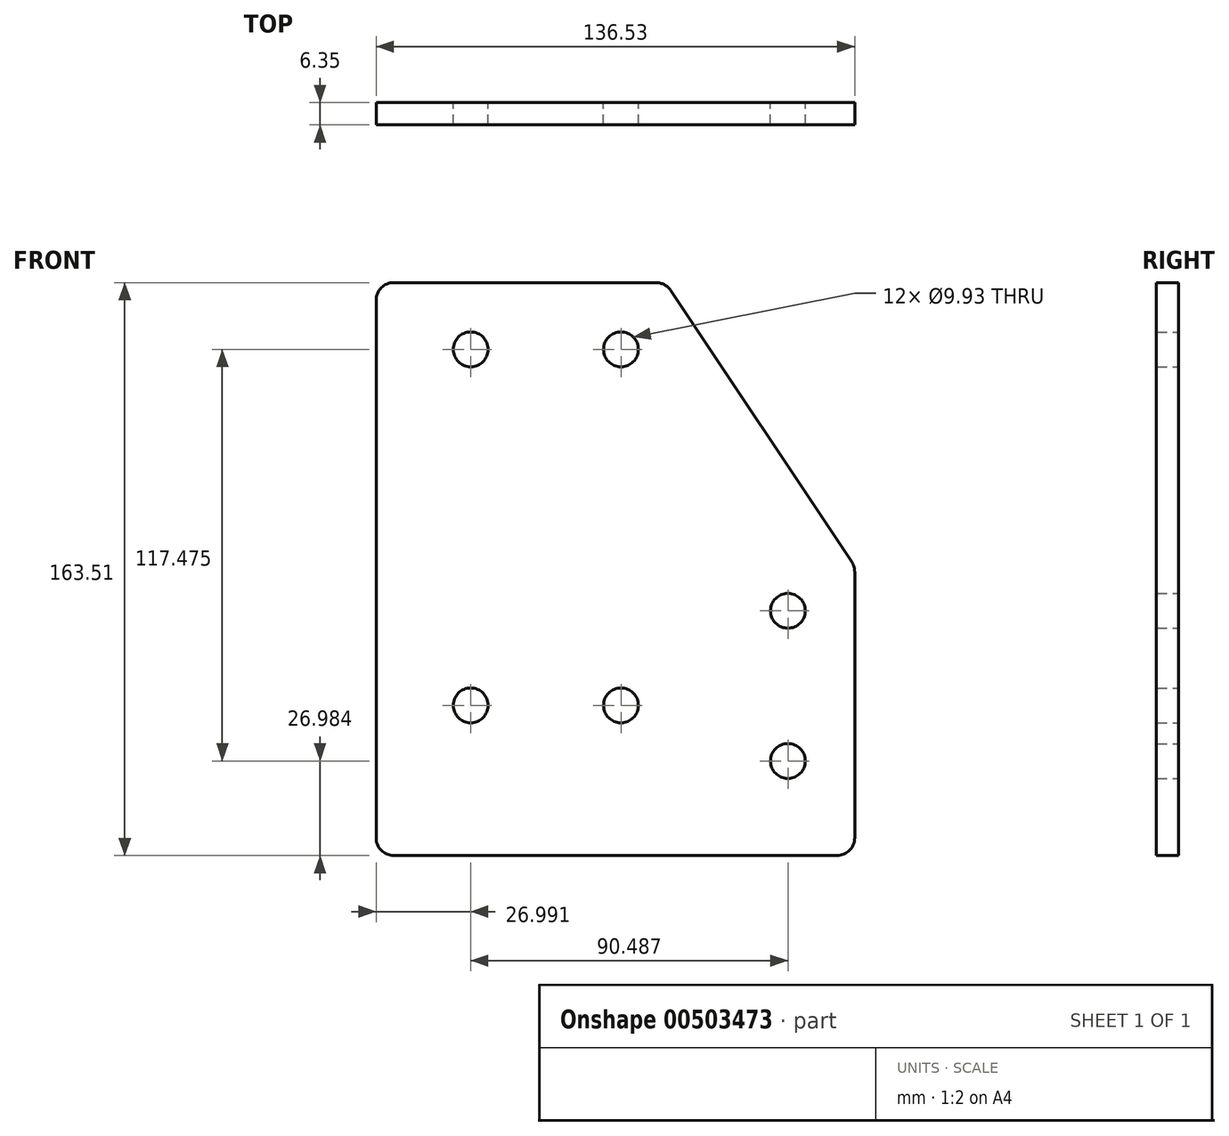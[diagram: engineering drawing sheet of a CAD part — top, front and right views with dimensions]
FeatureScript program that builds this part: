
annotation { "Feature Type Name" : "Feature", "Feature Type Description" : "" }
export const myFeature = defineFeature(function(context is Context, id is Id, definition is map)
    precondition{}
    {
        {
            var Q0;
            Q0=qCreatedBy(makeId("Front.planeOp"),FACE);
            var sketch = newSketch(context, id + "F0", { "sketchPlane" : qUnion([Q0])});
            skLineSegment(sketch, "E0.top", {"start": v(775.69, -334.6) * mm, "end": v(693.14, -334.6) * mm});
            skLineSegment(sketch, "E0.left", {"start": v(775.69, -471.13) * mm, "end": v(775.69, -334.6) * mm});
            skCircle(sketch, "E1", {"center": v(732.83, -444.14) * mm, "radius": 4.97 * mm});
            skCircle(sketch, "E2", {"center": v(732.83, -401.28) * mm, "radius": 4.97 * mm});
            skLineSegment(sketch, "E3", {"start": v(705.84, -353.65) * mm, "end": v(775.69, -353.65) * mm, "construction": true});
            skCircle(sketch, "E4", {"center": v(705.84, -353.65) * mm, "radius": 4.97 * mm});
            skCircle(sketch, "E5", {"center": v(748.7, -353.65) * mm, "radius": 4.97 * mm});
            skLineSegment(sketch, "E6", {"start": v(612.18, -471.13) * mm, "end": v(612.18, -388.58) * mm});
            skCircle(sketch, "E7", {"center": v(631.23, -444.14) * mm, "radius": 4.97 * mm});
            skCircle(sketch, "E8", {"center": v(631.23, -401.28) * mm, "radius": 4.97 * mm});
            skLineSegment(sketch, "E9", {"start": v(799.5, -319.6) * mm, "end": v(799.5, -500.26) * mm});
            skLineSegment(sketch, "E10", {"start": v(631.23, -444.14) * mm, "end": v(631.23, -494.94) * mm});
            skLineSegment(sketch, "E11", {"start": v(612.18, -471.13) * mm, "end": v(775.69, -471.13) * mm});
            skLineSegment(sketch, "E12", {"start": v(612.18, -388.58) * mm, "end": v(693.14, -334.6) * mm});
            skLineSegment(sketch, "E13.top", {"start": v(16.36, -0.2) * mm, "end": v(16.36, 82.36) * mm});
            skLineSegment(sketch, "E13.left", {"start": v(-120.17, -0.2) * mm, "end": v(16.36, -0.2) * mm});
            skCircle(sketch, "E14", {"center": v(-93.18, 42.67) * mm, "radius": 4.97 * mm});
            skCircle(sketch, "E15", {"center": v(-50.32, 42.67) * mm, "radius": 4.97 * mm});
            skLineSegment(sketch, "E16", {"start": v(-2.7, 69.66) * mm, "end": v(-2.7, -0.2) * mm, "construction": true});
            skCircle(sketch, "E17", {"center": v(-2.7, 69.66) * mm, "radius": 4.97 * mm});
            skCircle(sketch, "E18", {"center": v(-2.7, 26.8) * mm, "radius": 4.97 * mm});
            skLineSegment(sketch, "E19", {"start": v(-120.17, 163.32) * mm, "end": v(-37.62, 163.32) * mm});
            skCircle(sketch, "E20", {"center": v(-93.18, 144.27) * mm, "radius": 4.97 * mm});
            skCircle(sketch, "E21", {"center": v(-50.32, 144.27) * mm, "radius": 4.97 * mm});
            skLineSegment(sketch, "E22", {"start": v(31.37, -24) * mm, "end": v(-149.3, -24) * mm});
            skLineSegment(sketch, "E23", {"start": v(-93.18, 144.27) * mm, "end": v(-143.98, 144.27) * mm});
            skLineSegment(sketch, "E24", {"start": v(-120.17, 163.32) * mm, "end": v(-120.17, -0.2) * mm});
            skLineSegment(sketch, "E25", {"start": v(-37.62, 163.32) * mm, "end": v(16.36, 82.36) * mm});
            skSolve(sketch);
        }
        {
            var Q0;
            Q0=makeQuery(id+"F0.imprint","IMPRINT",FACE,{"disambiguationData":[TD([[makeQuery(id+"F0.imprint","IMPRINT",EDGE,{"derivedFrom":sQuery(id+"F0.wireOp",EDGE,"E13.top")}),1.0]])]});
            extrude(context, id + "F1", {"entities" : qUnion([Q0]), "depth" : 6.35 * mm, "offsetDistance" : 25.4 * mm});
        }
        {
            var Q0;
            Q0=makeQuery(id+"F1.opExtrude","SWEPT_EDGE",EDGE,{"disambiguationData":[OSD([sQuery(id+"FNj83cxcOXgbGo6_0.wireOp",EDGE,"YLJfwgbZ-YHyl-cvS9-Tr0C-U3R6be7mc2fx.top"),sQuery(id+"FNj83cxcOXgbGo6_0.wireOp",EDGE,"YLJfwgbZ-YHyl-cvS9-Tr0C-U3R6be7mc2fx.left")])]});
            var Q1;
            Q1=makeQuery(id+"F1.opExtrude","SWEPT_EDGE",EDGE,{"disambiguationData":[OSD([sQuery(id+"FNj83cxcOXgbGo6_0.wireOp",EDGE,"YLJfwgbZ-YHyl-cvS9-Tr0C-U3R6be7mc2fx.bottom"),sQuery(id+"FNj83cxcOXgbGo6_0.wireOp",EDGE,"YLJfwgbZ-YHyl-cvS9-Tr0C-U3R6be7mc2fx.left")])]});
            var Q2;
            Q2=makeQuery(id+"F1.opExtrude","SWEPT_EDGE",EDGE,{"disambiguationData":[OSD([sQuery(id+"FNj83cxcOXgbGo6_0.wireOp",EDGE,"YLJfwgbZ-YHyl-cvS9-Tr0C-U3R6be7mc2fx.bottom"),sQuery(id+"FNj83cxcOXgbGo6_0.wireOp",EDGE,"YLJfwgbZ-YHyl-cvS9-Tr0C-U3R6be7mc2fx.right")])]});
            var Q3;
            Q3=makeQuery(id+"F1.opExtrude","SWEPT_EDGE",EDGE,{"disambiguationData":[OSD([sQuery(id+"FNj83cxcOXgbGo6_0.wireOp",EDGE,"YLJfwgbZ-YHyl-cvS9-Tr0C-U3R6be7mc2fx.top"),sQuery(id+"FNj83cxcOXgbGo6_0.wireOp",EDGE,"YLJfwgbZ-YHyl-cvS9-Tr0C-U3R6be7mc2fx.right")])]});
            var Q4;
            Q4=makeQuery(id+"F1.opExtrude","SWEPT_EDGE",EDGE,{"disambiguationData":[OSD([sQuery(id+"FNj83cxcOXgbGo6_0.wireOp",EDGE,"av35LSo8-nv1P-ecUa-bM0M-DhvCoOtsW4H1"),sQuery(id+"FNj83cxcOXgbGo6_0.wireOp",EDGE,"TwLJLxqH-c4EN-Iaun-qm5o-bjvqboWOfFqz")])]});
            var Q5;
            Q5=makeQuery(id+"F1.opExtrude","SWEPT_EDGE",EDGE,{"disambiguationData":[OSD([sQuery(id+"FNj83cxcOXgbGo6_0.wireOp",EDGE,"TwLJLxqH-c4EN-Iaun-qm5o-bjvqboWOfFqz"),sQuery(id+"FNj83cxcOXgbGo6_0.wireOp",EDGE,"qYVnyuXa-Kr3J-J92z-Ydc9-I5E6tiZ9RHag")])]});
            var Q6;
            Q6=makeQuery(id+"F1.opExtrude","SWEPT_EDGE",EDGE,{"disambiguationData":[OSD([sQuery(id+"F0.wireOp",EDGE,"E19"),sQuery(id+"F0.wireOp",EDGE,"E25")])]});
            var Q7;
            Q7=makeQuery(id+"F1.opExtrude","SWEPT_EDGE",EDGE,{"disambiguationData":[OSD([sQuery(id+"F0.wireOp",EDGE,"E13.top"),sQuery(id+"F0.wireOp",EDGE,"E25")])]});
            var Q8;
            Q8=makeQuery(id+"F1.opExtrude","SWEPT_EDGE",EDGE,{"disambiguationData":[OSD([sQuery(id+"F0.wireOp",EDGE,"E13.top"),sQuery(id+"F0.wireOp",EDGE,"E13.left")])]});
            var Q9;
            Q9=makeQuery(id+"F1.opExtrude","SWEPT_EDGE",EDGE,{"disambiguationData":[OSD([sQuery(id+"F0.wireOp",EDGE,"E13.left"),sQuery(id+"F0.wireOp",EDGE,"E24")])]});
            var Q10;
            Q10=makeQuery(id+"F1.opExtrude","SWEPT_EDGE",EDGE,{"disambiguationData":[OSD([sQuery(id+"F0.wireOp",EDGE,"E19"),sQuery(id+"F0.wireOp",EDGE,"E24")])]});
            fillet(context, id + "F2", {"entities" : qUnion([Q0, Q1, Q2, Q3, Q4, Q5, Q6, Q7, Q8, Q9, Q10]), "radius" : 5.08 * mm, "tangentPropagation" : true, "allowEdgeOverflow" : false});
        }
    });
